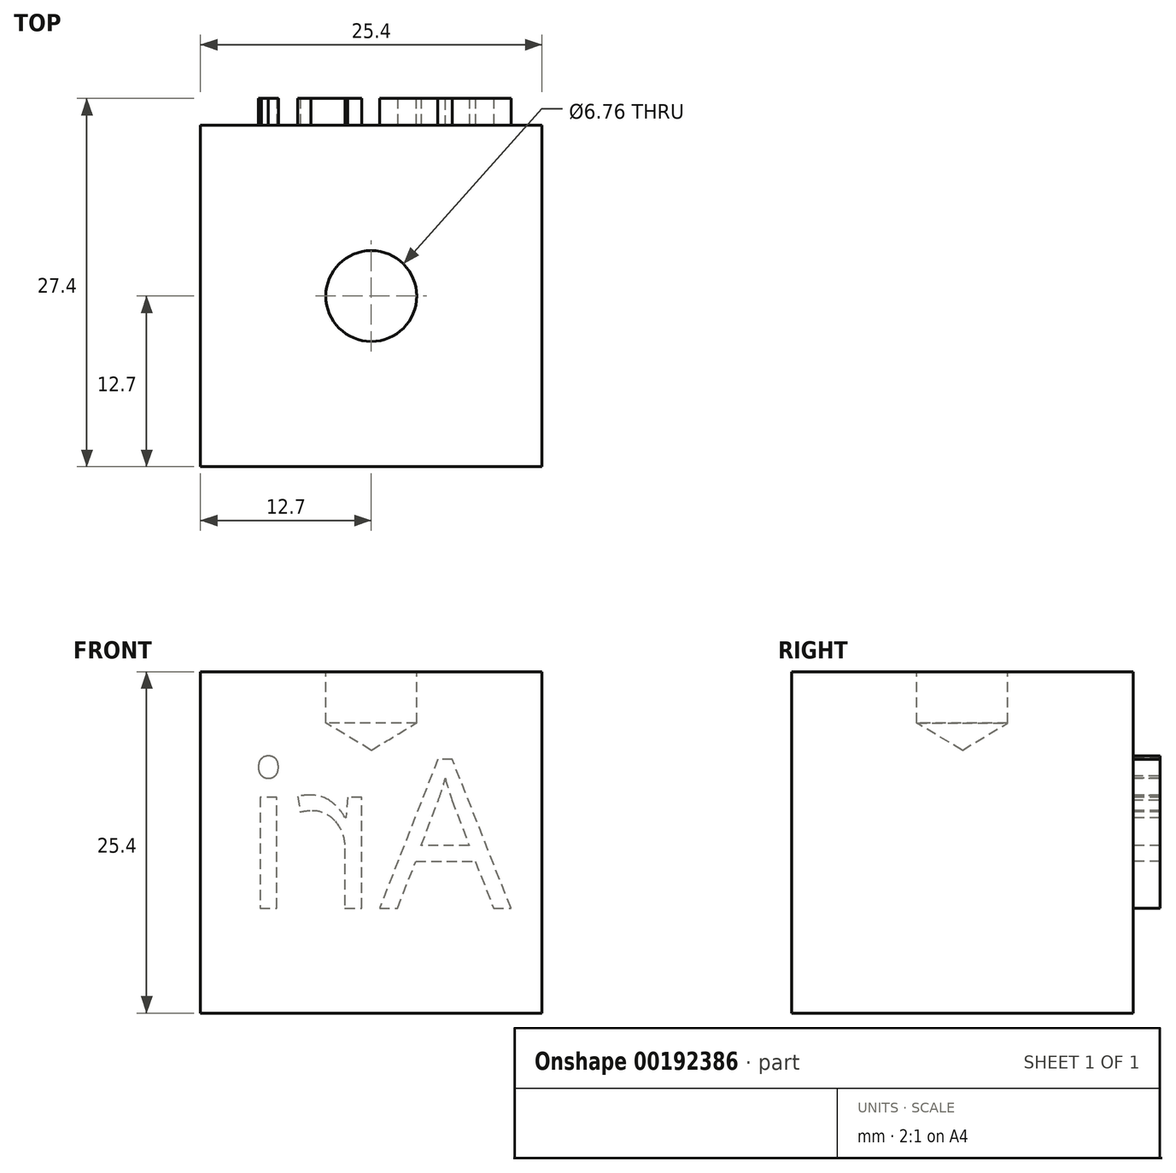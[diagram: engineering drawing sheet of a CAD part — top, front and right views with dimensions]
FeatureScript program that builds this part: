
annotation { "Feature Type Name" : "Feature", "Feature Type Description" : "" }
export const myFeature = defineFeature(function(context is Context, id is Id, definition is map)
    precondition{}
    {
        {
            var Q0;
            Q0=qCreatedBy(makeId("Front.planeOp"),FACE);
            var sketch = newSketch(context, id + "F0", { "sketchPlane" : qUnion([Q0])});
            skLineSegment(sketch, "E0.bottom", {"start": v(-12.7, 12.7) * mm, "end": v(12.7, 12.7) * mm});
            skLineSegment(sketch, "E0.top", {"start": v(-12.7, -12.7) * mm, "end": v(12.7, -12.7) * mm});
            skLineSegment(sketch, "E0.left", {"start": v(-12.7, 12.7) * mm, "end": v(-12.7, -12.7) * mm});
            skLineSegment(sketch, "E0.right", {"start": v(12.7, 12.7) * mm, "end": v(12.7, -12.7) * mm});
            skPoint(sketch, "E0.middle", {"position": v(0, 0) * mm});
            skSolve(sketch);
        }
        {
            var Q0;
            Q0=makeQuery(id+"F0.imprint","IMPRINT",FACE,{"disambiguationData":[TD([[makeQuery(id+"F0.imprint","IMPRINT",EDGE,{"derivedFrom":sQuery(id+"F0.wireOp",EDGE,"E0.bottom")}),-1.0]])]});
            extrude(context, id + "F1", {"entities" : qUnion([Q0]), "endBound" : BoundingType.SYMMETRIC, "depth" : 25.4 * mm});
        }
        {
            var Q0;
            Q0=makeQuery(id+"F1.opExtrude","SWEPT_FACE",FACE,{"disambiguationData":[OSD([sQuery(id+"F0.wireOp",EDGE,"E0.bottom")])]});
            var sketch = newSketch(context, id + "F2", { "sketchPlane" : qUnion([Q0])});
            skPoint(sketch, "E1", {"position": v(0, 0) * mm});
            skSolve(sketch);
        }
        {
            var Q0;
            Q0=sQuery(id+"F2.wireOp",VERTEX,"E1");
            var Q1;
            Q1=makeQuery(id+"F1.opExtrude","SWEPT_BODY",BODY,{"disambiguationData":[OSD([sQuery(id+"F0.wireOp",EDGE,"E0.bottom"),sQuery(id+"F0.wireOp",EDGE,"E0.top"),sQuery(id+"F0.wireOp",EDGE,"E0.left"),sQuery(id+"F0.wireOp",EDGE,"E0.right")])]});
            hole(context, id + "F3", {"style" : HoleStyle.SIMPLE, "endStyle" : HoleEndStyle.BLIND, "holeDiameter" : 6.76 * mm, "holeDepth" : 3.8 * mm, "locations" : qUnion([Q0]), "scope" : qUnion([Q1])});
        }
        {
            var Q0;
            Q0=makeQuery(id+"F1.opExtrude","CAP_FACE",FACE,{"disambiguationData":[OSD([sQuery(id+"F0.wireOp",EDGE,"E0.bottom"),sQuery(id+"F0.wireOp",EDGE,"E0.top"),sQuery(id+"F0.wireOp",EDGE,"E0.left"),sQuery(id+"F0.wireOp",EDGE,"E0.right")])],"isStart":true});
            var sketch = newSketch(context, id + "F4", { "sketchPlane" : qUnion([Q0])});
            skText(sketch, "E2", { "text": "Ari\n", "fontName": "OpenSans-Regular.ttf"});
            const initialGuessF4  = {"E2": [-0.01039, -0.0049, 1, 0, 0.01112]};
            skSetInitialGuess(sketch, initialGuessF4);
            skSolve(sketch);
        }
        {
            var Q0;
            Q0 = qSketchRegion(id + "F4", true);
            extrude(context, id + "F5", {"entities" : qUnion([Q0]), "operationType" : NewBodyOperationType.ADD, "depth" : 2 * mm});
        }
    });
